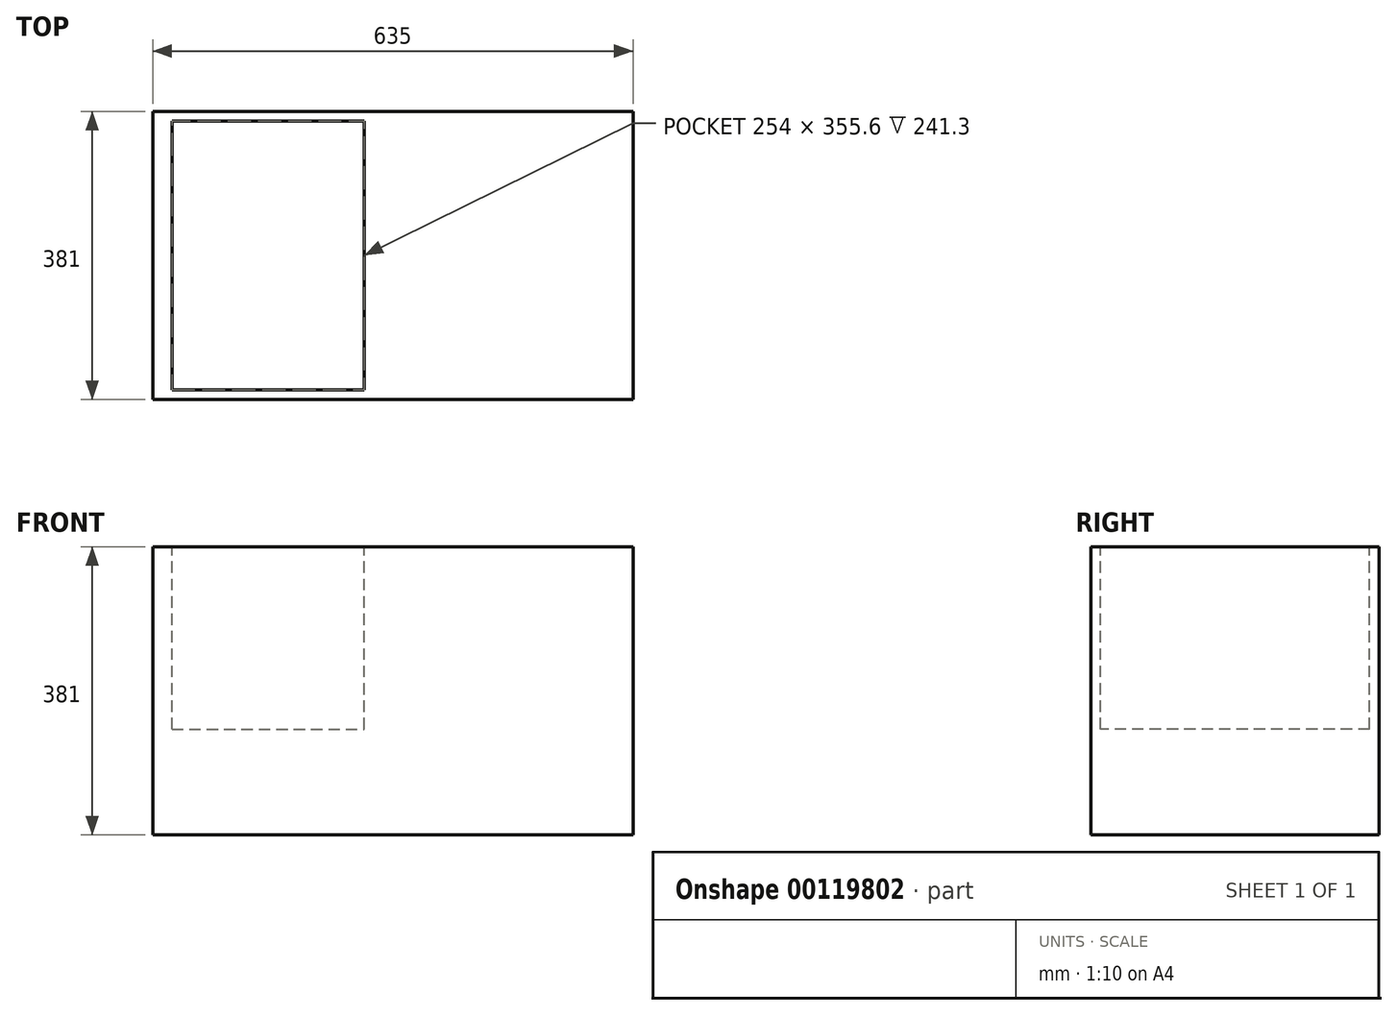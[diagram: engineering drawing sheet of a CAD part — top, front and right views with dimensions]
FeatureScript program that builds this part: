
annotation { "Feature Type Name" : "Feature", "Feature Type Description" : "" }
export const myFeature = defineFeature(function(context is Context, id is Id, definition is map)
    precondition{}
    {
        {
            var Q0;
            Q0=qCreatedBy(makeId("Front.planeOp"),FACE);
            var sketch = newSketch(context, id + "F0", { "sketchPlane" : qUnion([Q0])});
            skLineSegment(sketch, "E0.bottom", {"start": v(-377.6, 227.79) * mm, "end": v(257.4, 227.79) * mm});
            skLineSegment(sketch, "E0.top", {"start": v(-377.6, -153.21) * mm, "end": v(257.4, -153.21) * mm});
            skLineSegment(sketch, "E0.left", {"start": v(-377.6, 227.79) * mm, "end": v(-377.6, -153.21) * mm});
            skLineSegment(sketch, "E0.right", {"start": v(257.4, 227.79) * mm, "end": v(257.4, -153.21) * mm});
            skSolve(sketch);
        }
        {
            var Q0;
            Q0 = qSketchRegion(id + "F0", true);
            extrude(context, id + "F1", {"entities" : qUnion([Q0]), "depth" : 381 * mm});
        }
        {
            var Q0;
            Q0=makeQuery(id+"F1.opExtrude","SWEPT_FACE",FACE,{"disambiguationData":[OSD([sQuery(id+"F0.wireOp",EDGE,"E0.bottom")])]});
            var sketch = newSketch(context, id + "F2", { "sketchPlane" : qUnion([Q0])});
            skLineSegment(sketch, "E1.bottom", {"start": v(-352.2, -12.7) * mm, "end": v(-98.2, -12.7) * mm});
            skLineSegment(sketch, "E1.top", {"start": v(-352.2, -368.3) * mm, "end": v(-98.2, -368.3) * mm});
            skLineSegment(sketch, "E1.left", {"start": v(-352.2, -12.7) * mm, "end": v(-352.2, -368.3) * mm});
            skLineSegment(sketch, "E1.right", {"start": v(-98.2, -12.7) * mm, "end": v(-98.2, -368.3) * mm});
            skSolve(sketch);
        }
        {
            var Q0;
            Q0=makeQuery(id+"F2.imprint","IMPRINT",FACE,{"disambiguationData":[TD([[makeQuery(id+"F2.imprint","IMPRINT",EDGE,{"derivedFrom":sQuery(id+"F2.wireOp",EDGE,"E1.bottom")}),-1.0]])]});
            extrude(context, id + "F3", {"entities" : qUnion([Q0]), "operationType" : NewBodyOperationType.REMOVE, "oppositeDirection" : true, "depth" : 241.3 * mm});
        }
    });
